# Revit family: Reece_Vanity_Posh_Domaine
name_source: partatom
category: Casework
revit_build: Autodesk Revit 2018 (Build: 20190510_1515(x64)
units: mm (PartAtom-declared; Revit-internal decimal feet)

## family parameters
Always vertical = Yes
Cut with Voids When Loaded = Yes
Room Calculation Point = No
Shared = Yes
Work Plane-Based = Yes

## types (1)
- Reece_All_Types
    Construction Type = Casework
    Default Elevation = 0 mm  [stored 0 ft]
    Depth = 460 mm  [stored 1.50919 ft]
    Description = -
    Disclaimer = THIS FILE IS THE PROPERTY OF THE REECE GROUP. IT MAY NOT BE REPRODUCED, REVERSE-ENGINEERED OR MODIFIED. ANY REPUBLICATION, TRANSMISSION OR DISTRIBUTION FOR THE PURPOSE OF COMMERCIALLY EXPLOITING THE FILES IS PROHIBITED.
    Finish = Please refer to Colour, Finish and Material Variations Document for more information.
    Height = 22 mm  [stored 0.0721785 ft]
    Keynote = Product #, Reece_Vanity_Posh_Domaine - Reece_All_Types
    Manufacturer = Posh
    Model = Domaine
    Panel_Type 5_Twin Drawers = No
    Panel_Type_1 = No
    Panel_Type_2_Twin = No
    Panel_Type_3_Open Shelf = No
    Reece_Attachment Point_Offset = 450 mm  [stored 1.47638 ft]
    Reece_Attachment_Point = Yes
    Reece_Attachment_Point_1 = No
    Reece_Attachment_Point_2 = Yes
    Reece_Basin_Depth_Type 1-2 = 280 mm  [stored 0.918635 ft]
    Reece_Basin_Depth_Type 3 = 192 mm  [stored 0.629921 ft]
    Reece_Basin_Outlet_Type 1_Benchtop = 0 mm  [stored 0 ft]
    Reece_Basin_Outlet_Type 2_Benchtop = 0 mm  [stored 0 ft]
    Reece_Basin_Outlet_Type 3_Benchtop = 0 mm  [stored 0 ft]
    Reece_Basin_Outlet_Type 4_Benchtop = 0 mm  [stored 0 ft]
    Reece_Basin_Outlet_Type 5_Benchtop = 0 mm  [stored 0 ft]
    Reece_Basin_Outlet_Type 6_Benchtop = 0 mm  [stored 0 ft]
    Reece_Basin_Outlet_Type 7_Left_Benchtop = 0 mm  [stored 0 ft]
    Reece_Basin_Outlet_Type 7_Right_Benchtop = 0 mm  [stored 0 ft]
    Reece_Detail_Additional = Please refer to Colour, Finish and Material Variations Document for more information.
    Reece_Detail_Disclaimer = THIS FILE IS THE PROPERTY OF THE REECE GROUP. IT MAY NOT BE REPRODUCED, REVERSE-ENGINEERED OR MODIFIED. ANY REPUBLICATION, TRANSMISSION OR DISTRIBUTION FOR THE PURPOSE OF COMMERCIALLY EXPLOITING THE FILES IS PROHIBITED.
    Reece_Drawer_Count = 3
    Reece_Drawer_Count_Limit = 3
    Reece_Drawer_Cut Width = 130 mm  [stored 0.426509 ft]
    Reece_Drawer_Height = 752 mm  [stored 2.46719 ft]
    Reece_Drawer_Height_2 = 251 mm  [stored 0.823491 ft]
    Reece_Drawer_Height_3 = 232 mm  [stored 0.761155 ft]
    Reece_Drawer_Offset 1 = 50 mm  [stored 0.164042 ft]
    Reece_Drawer_Offset 2 = 50 mm  [stored 0.164042 ft]
    Reece_Drawer_Visibility = No
    Reece_Drawer_Visibility_2 = Yes
    Reece_Drawers_Offset = 275 mm
    Reece_Floor_Mount = Yes
    Reece_Front Panel_Count = 4
    Reece_Material_Benchtop = Reece_Cast_Marble_White
    Reece_Material_Cabinet = Reece_Silk_Polar_Matte White
    Reece_Material_Colour = Reece_Silk_Polar_Matte White
    Reece_Material_Secondary = Reece_Brass_Chrome
    Reece_Mini Basin_Switch = No
    Reece_No Basin = 0 mm  [stored 0 ft]
    Reece_Panel_Count_Doors = 4
    Reece_Panel_Gap = 2 mm  [stored 0.00656168 ft]
    Reece_Panel_Thickness_Back = 16 mm  [stored 0.0524934 ft]
    Reece_Panel_Thickness_Bottom = 16 mm  [stored 0.0524934 ft]
    Reece_Panel_Thickness_Side = 16 mm  [stored 0.0524934 ft]
    Reece_Panel_Thickness_Top = 22 mm  [stored 0.0721785 ft]
    Reece_Panels_Count = 4
    Reece_Product_Brand = Posh
    Reece_Product_Sub Brand = Domaine
    Reece_Product_Type = Vanity
    Reece_Product_Web Page = https://www.reece.com.au
    Reece_Top_Strip = Yes
    Reece_Type 1_Benchtop = No
    Reece_Type 2_Benchtop = No
    Reece_Type 3_Benchtop = No
    Reece_Type 4_Benchtop = No
    Reece_Type 5_Benchtop = Yes
    Reece_Type 5_Central Panel Width = 495 mm  [stored 1.62402 ft]
    Reece_Type 5_Panel Width = 394 mm
    Reece_Type 6_Benchtop = No
    Reece_Type 7_Benchtop_Left = No
    Reece_Type 7_Benchtop_Right = No
    Reece_Vanity_Bowl_Count = 2
    Reece_Vanity_Cabinet_Depth = 434 mm  [stored 1.42388 ft]
    Reece_Vanity_Cabinet_Height = 780 mm  [stored 2.55906 ft]
    Reece_Vanity_Cabinet_Width = 1788 mm
    Reece_Vanity_Centre_Bowl = No
    Reece_Vanity_Double_Bowl = Yes
    Reece_Vanity_Top_Depth = 460 mm  [stored 1.50919 ft]
    Reece_Vanity_Top_Width = 1800 mm  [stored 5.90551 ft]
    Type 1_Benchtop_Cast Marble Single = No
    Type 2_Benchtop_Cast Marble Double = No
    Type 3_Benchtop_Ceramic Single = No
    Type 4_Benchtop_Ceramic Double = No
    Type 5_Benchtop = Yes
    Type 6_Benchtop_Mini = No
    Type 7_Benchtop_Left Offset = No
    Type 7_Benchtop_Right Offset = No
    Type Comments = Vanity
    URL = https://www.reece.com.au
    Width = 1800 mm  [stored 5.90551 ft]

note: [stored X ft] marks values corroborated as IEEE doubles in the binary element streams (Revit-internal decimal feet)

## geometry (parser evidence)
native form markers: Sweep x22
no freeform markers — native parametric forms only
